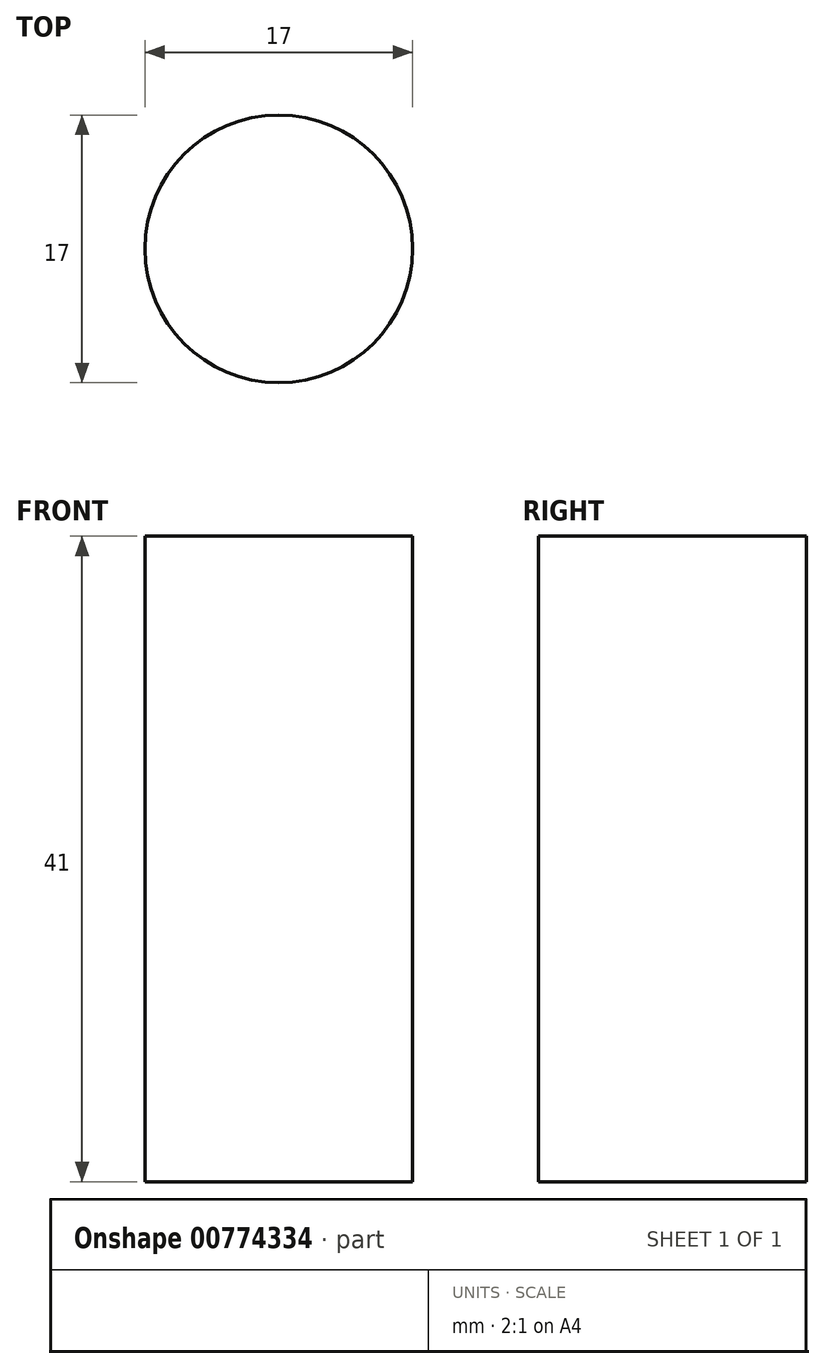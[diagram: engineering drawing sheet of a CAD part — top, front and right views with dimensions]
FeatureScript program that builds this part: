
annotation { "Feature Type Name" : "Feature", "Feature Type Description" : "" }
export const myFeature = defineFeature(function(context is Context, id is Id, definition is map)
    precondition{}
    {
        {
            var Q0;
            Q0=qCreatedBy(makeId("Top.planeOp"),FACE);
            var sketch = newSketch(context, id + "F0", { "sketchPlane" : qUnion([Q0])});
            skCircle(sketch, "E0", {"center": v(0, -5) * mm, "radius": 8.5 * mm});
            skSolve(sketch);
        }
        {
            var Q0;
            Q0 = qSketchRegion(id + "F0", true);
            extrude(context, id + "F1", {"entities" : qUnion([Q0]), "oppositeDirection" : true, "depth" : 41 * mm, "offsetDistance" : 25 * mm});
        }
    });
